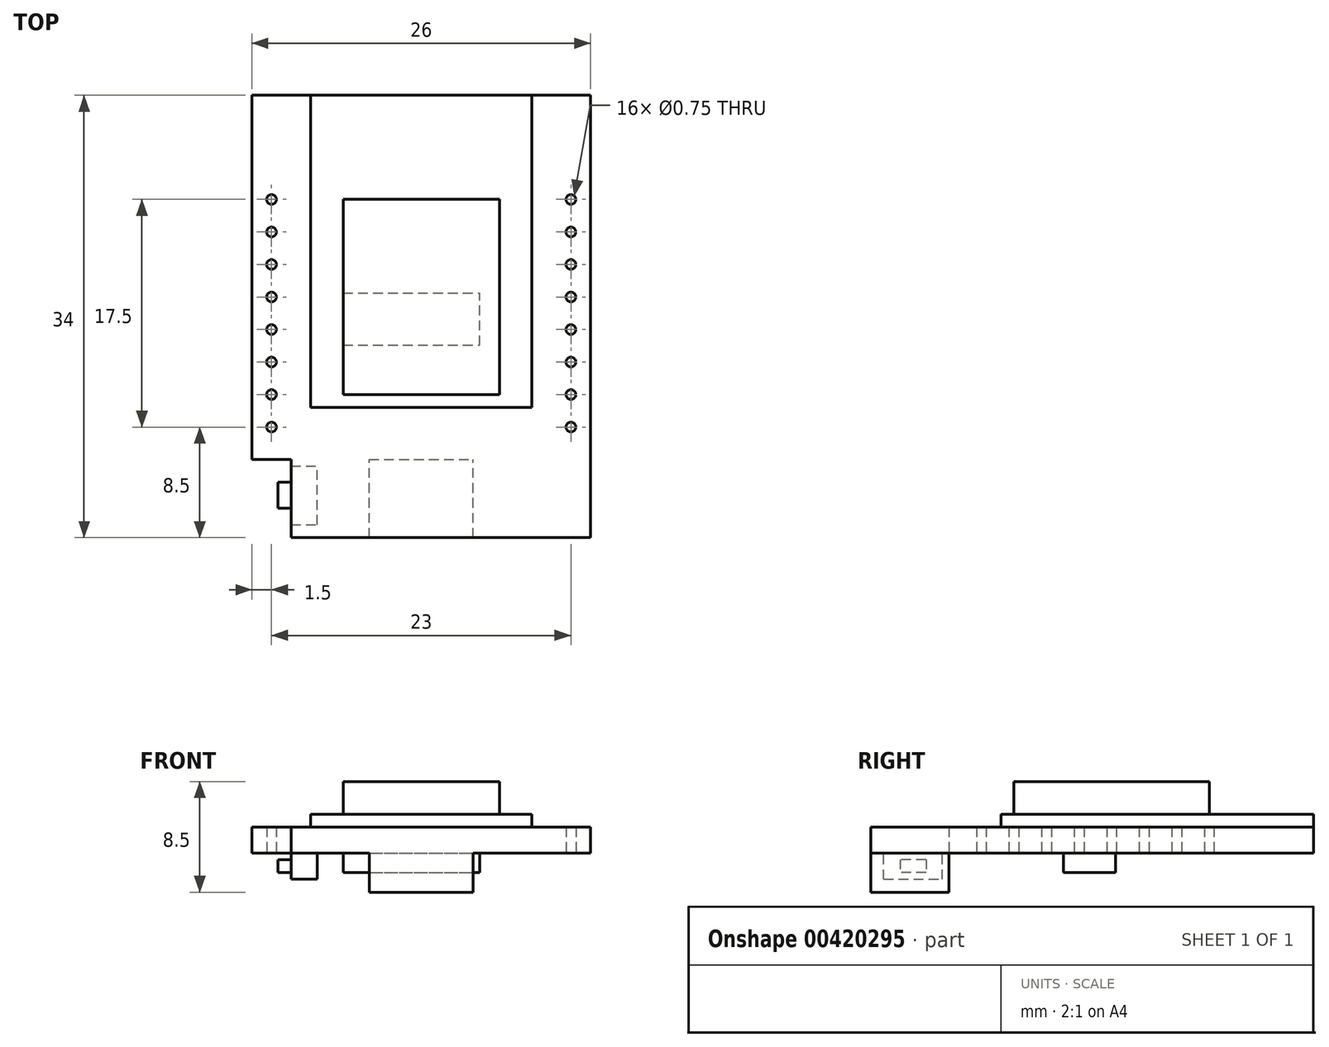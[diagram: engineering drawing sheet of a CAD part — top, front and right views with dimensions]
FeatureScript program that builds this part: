
annotation { "Feature Type Name" : "Feature", "Feature Type Description" : "" }
export const myFeature = defineFeature(function(context is Context, id is Id, definition is map)
    precondition{}
    {
        {
            var Q0;
            Q0=qCreatedBy(makeId("Top.planeOp"),FACE);
            var sketch = newSketch(context, id + "F0", { "sketchPlane" : qUnion([Q0])});
            skLineSegment(sketch, "E0.bottom", {"start": v(-13, 17) * mm, "end": v(13, 17) * mm});
            skLineSegment(sketch, "E0.top", {"start": v(-10, -17) * mm, "end": v(13, -17) * mm});
            skLineSegment(sketch, "E0.left", {"start": v(-13, 17) * mm, "end": v(-13, -11) * mm});
            skLineSegment(sketch, "E0.right", {"start": v(13, 17) * mm, "end": v(13, -17) * mm});
            skLineSegment(sketch, "E1.top", {"start": v(-13, -11) * mm, "end": v(-10, -11) * mm});
            skLineSegment(sketch, "E1.right", {"start": v(-10, -17) * mm, "end": v(-10, -11) * mm});
            skSolve(sketch);
        }
        {
            var Q0;
            Q0=qSketchRegion(id+"F0",true);
            extrude(context, id + "F1", {"entities" : qUnion([Q0]), "depth" : 2 * mm});
        }
        {
            var Q0;
            Q0=makeQuery(id+"F1.opExtrude","CAP_FACE",FACE,{"disambiguationData":[OSD([sQuery(id+"F0.wireOp",EDGE,"E0.bottom"),sQuery(id+"F0.wireOp",EDGE,"E0.top"),sQuery(id+"F0.wireOp",EDGE,"E0.left"),sQuery(id+"F0.wireOp",EDGE,"E0.right"),sQuery(id+"F0.wireOp",EDGE,"E1.bottom"),sQuery(id+"F0.wireOp",EDGE,"E1.left")])],"isStart":false});
            var sketch = newSketch(context, id + "F2", { "sketchPlane" : qUnion([Q0])});
            skLineSegment(sketch, "E2.bottom", {"start": v(-8.5, 17) * mm, "end": v(8.5, 17) * mm});
            skLineSegment(sketch, "E2.top", {"start": v(-8.5, -7) * mm, "end": v(8.5, -7) * mm});
            skLineSegment(sketch, "E2.left", {"start": v(-8.5, 17) * mm, "end": v(-8.5, -7) * mm});
            skLineSegment(sketch, "E2.right", {"start": v(8.5, 17) * mm, "end": v(8.5, -7) * mm});
            skSolve(sketch);
        }
        {
            var Q0;
            Q0=qSketchRegion(id+"F2",true);
            extrude(context, id + "F3", {"entities" : qUnion([Q0]), "operationType" : NewBodyOperationType.ADD, "depth" : 1 * mm});
        }
        {
            var Q0;
            Q0=makeQuery(id+"F3.opExtrude","CAP_FACE",FACE,{"disambiguationData":[OSD([sQuery(id+"F2.wireOp",EDGE,"E2.bottom"),sQuery(id+"F2.wireOp",EDGE,"E2.top"),sQuery(id+"F2.wireOp",EDGE,"E2.left"),sQuery(id+"F2.wireOp",EDGE,"E2.right")])],"isStart":false});
            var sketch = newSketch(context, id + "F4", { "sketchPlane" : qUnion([Q0])});
            skLineSegment(sketch, "E3.bottom", {"start": v(-6, 9) * mm, "end": v(6, 9) * mm});
            skLineSegment(sketch, "E3.top", {"start": v(-6, -6) * mm, "end": v(6, -6) * mm});
            skLineSegment(sketch, "E3.left", {"start": v(-6, 9) * mm, "end": v(-6, -6) * mm});
            skLineSegment(sketch, "E3.right", {"start": v(6, 9) * mm, "end": v(6, -6) * mm});
            skSolve(sketch);
        }
        {
            var Q0;
            Q0=qSketchRegion(id+"F4",true);
            extrude(context, id + "F5", {"entities" : qUnion([Q0]), "operationType" : NewBodyOperationType.ADD, "depth" : 2.5 * mm});
        }
        {
            var Q0;
            Q0=makeQuery(id+"F1.opExtrude","CAP_FACE",FACE,{"disambiguationData":[OSD([sQuery(id+"F0.wireOp",EDGE,"E0.bottom"),sQuery(id+"F0.wireOp",EDGE,"E0.top"),sQuery(id+"F0.wireOp",EDGE,"E0.left"),sQuery(id+"F0.wireOp",EDGE,"E0.right"),sQuery(id+"F0.wireOp",EDGE,"E1.top"),sQuery(id+"F0.wireOp",EDGE,"E1.right")])],"isStart":true});
            var sketch = newSketch(context, id + "F6", { "sketchPlane" : qUnion([Q0])});
            skLineSegment(sketch, "E4.bottom", {"start": v(-4, 17) * mm, "end": v(4, 17) * mm});
            skLineSegment(sketch, "E4.top", {"start": v(-4, 11) * mm, "end": v(4, 11) * mm});
            skLineSegment(sketch, "E4.left", {"start": v(-4, 17) * mm, "end": v(-4, 11) * mm});
            skLineSegment(sketch, "E4.right", {"start": v(4, 17) * mm, "end": v(4, 11) * mm});
            skSolve(sketch);
        }
        {
            var Q0;
            Q0=qSketchRegion(id+"F6",true);
            extrude(context, id + "F7", {"entities" : qUnion([Q0]), "operationType" : NewBodyOperationType.ADD, "depth" : 3 * mm});
        }
        {
            var Q0;
            Q0=makeQuery(id+"F1.opExtrude","CAP_FACE",FACE,{"disambiguationData":[OSD([sQuery(id+"F0.wireOp",EDGE,"E0.bottom"),sQuery(id+"F0.wireOp",EDGE,"E0.top"),sQuery(id+"F0.wireOp",EDGE,"E0.left"),sQuery(id+"F0.wireOp",EDGE,"E0.right"),sQuery(id+"F0.wireOp",EDGE,"E1.top"),sQuery(id+"F0.wireOp",EDGE,"E1.right")])],"isStart":true});
            var sketch = newSketch(context, id + "F8", { "sketchPlane" : qUnion([Q0])});
            skLineSegment(sketch, "E5.bottom", {"start": v(-10, 16) * mm, "end": v(-8, 16) * mm});
            skLineSegment(sketch, "E5.top", {"start": v(-10, 11.5) * mm, "end": v(-8, 11.5) * mm});
            skLineSegment(sketch, "E5.left", {"start": v(-10, 16) * mm, "end": v(-10, 11.5) * mm});
            skLineSegment(sketch, "E5.right", {"start": v(-8, 16) * mm, "end": v(-8, 11.5) * mm});
            skSolve(sketch);
        }
        {
            var Q0;
            Q0=qSketchRegion(id+"F8",true);
            extrude(context, id + "F9", {"entities" : qUnion([Q0]), "operationType" : NewBodyOperationType.ADD, "depth" : 2 * mm});
        }
        {
            var Q0;
            Q0=makeQuery(id+"F9.boolean.opBoolean","MERGE",FACE,{"derivedFrom":[makeQuery(id+"F1.opExtrude","SWEPT_FACE",FACE,{"disambiguationData":[OSD([sQuery(id+"F0.wireOp",EDGE,"E1.right")])]}),makeQuery(id+"F9.opExtrude","SWEPT_FACE",FACE,{"disambiguationData":[OSD([sQuery(id+"F8.wireOp",EDGE,"E5.left")])]})]});
            var sketch = newSketch(context, id + "F10", { "sketchPlane" : qUnion([Q0])});
            skLineSegment(sketch, "E6.bottom", {"start": v(12.75, -0.5) * mm, "end": v(14.75, -0.5) * mm});
            skLineSegment(sketch, "E6.top", {"start": v(12.75, -1.5) * mm, "end": v(14.75, -1.5) * mm});
            skLineSegment(sketch, "E6.left", {"start": v(12.75, -0.5) * mm, "end": v(12.75, -1.5) * mm});
            skLineSegment(sketch, "E6.right", {"start": v(14.75, -0.5) * mm, "end": v(14.75, -1.5) * mm});
            skSolve(sketch);
        }
        {
            var Q0;
            Q0=qSketchRegion(id+"F10",true);
            extrude(context, id + "F11", {"entities" : qUnion([Q0]), "operationType" : NewBodyOperationType.ADD, "depth" : 1 * mm});
        }
        {
            var Q0;
            Q0=makeQuery(id+"F1.opExtrude","CAP_FACE",FACE,{"disambiguationData":[OSD([sQuery(id+"F0.wireOp",EDGE,"E0.bottom"),sQuery(id+"F0.wireOp",EDGE,"E0.top"),sQuery(id+"F0.wireOp",EDGE,"E0.left"),sQuery(id+"F0.wireOp",EDGE,"E0.right"),sQuery(id+"F0.wireOp",EDGE,"E1.top"),sQuery(id+"F0.wireOp",EDGE,"E1.right")])],"isStart":true});
            var sketch = newSketch(context, id + "F12", { "sketchPlane" : qUnion([Q0])});
            skLineSegment(sketch, "E7.bottom", {"start": v(-6, 2.2) * mm, "end": v(4.5, 2.2) * mm});
            skLineSegment(sketch, "E7.top", {"start": v(-6, -1.8) * mm, "end": v(4.5, -1.8) * mm});
            skLineSegment(sketch, "E7.left", {"start": v(-6, 2.2) * mm, "end": v(-6, -1.8) * mm});
            skLineSegment(sketch, "E7.right", {"start": v(4.5, 2.2) * mm, "end": v(4.5, -1.8) * mm});
            skSolve(sketch);
        }
        {
            var Q0;
            Q0=qSketchRegion(id+"F12",true);
            extrude(context, id + "F13", {"entities" : qUnion([Q0]), "operationType" : NewBodyOperationType.ADD, "depth" : 1.5 * mm});
        }
        {
            var Q0;
            Q0=makeQuery(id+"F1.opExtrude","CAP_FACE",FACE,{"disambiguationData":[OSD([sQuery(id+"F0.wireOp",EDGE,"E0.bottom"),sQuery(id+"F0.wireOp",EDGE,"E0.top"),sQuery(id+"F0.wireOp",EDGE,"E0.left"),sQuery(id+"F0.wireOp",EDGE,"E0.right"),sQuery(id+"F0.wireOp",EDGE,"E1.top"),sQuery(id+"F0.wireOp",EDGE,"E1.right")])],"isStart":true});
            var sketch = newSketch(context, id + "F14", { "sketchPlane" : qUnion([Q0])});
            skCircle(sketch, "E8", {"center": v(-11.5, -9) * mm, "radius": 0.38 * mm});
            skCircle(sketch, "E9.0.1.0", {"center": v(-11.5, -6.5) * mm, "radius": 0.38 * mm});
            skCircle(sketch, "E9.0.2.0", {"center": v(-11.5, -4) * mm, "radius": 0.38 * mm});
            skCircle(sketch, "E9.0.3.0", {"center": v(-11.5, -1.5) * mm, "radius": 0.38 * mm});
            skCircle(sketch, "E9.0.4.0", {"center": v(-11.5, 1) * mm, "radius": 0.38 * mm});
            skCircle(sketch, "E9.0.5.0", {"center": v(-11.5, 3.5) * mm, "radius": 0.38 * mm});
            skCircle(sketch, "E9.0.6.0", {"center": v(-11.5, 6) * mm, "radius": 0.38 * mm});
            skCircle(sketch, "E9.0.7.0", {"center": v(-11.5, 8.5) * mm, "radius": 0.38 * mm});
            skLineSegment(sketch, "E9.direction1", {"start": v(-11.5, -9) * mm, "end": v(11.5, -9) * mm, "construction": true});
            skLineSegment(sketch, "E9.direction2", {"start": v(-11.5, -9) * mm, "end": v(-11.5, -6.5) * mm, "construction": true});
            skCircle(sketch, "E10.0.1.0", {"center": v(11.5, -9) * mm, "radius": 0.38 * mm});
            skCircle(sketch, "E10.0.1.1", {"center": v(11.5, -6.5) * mm, "radius": 0.38 * mm});
            skCircle(sketch, "E10.0.1.2", {"center": v(11.5, -4) * mm, "radius": 0.38 * mm});
            skCircle(sketch, "E10.0.1.3", {"center": v(11.5, -1.5) * mm, "radius": 0.38 * mm});
            skCircle(sketch, "E10.0.1.4", {"center": v(11.5, 1) * mm, "radius": 0.38 * mm});
            skCircle(sketch, "E10.0.1.5", {"center": v(11.5, 3.5) * mm, "radius": 0.38 * mm});
            skCircle(sketch, "E10.0.1.6", {"center": v(11.5, 6) * mm, "radius": 0.38 * mm});
            skCircle(sketch, "E10.0.1.7", {"center": v(11.5, 8.5) * mm, "radius": 0.38 * mm});
            skSolve(sketch);
        }
        {
            var Q0;
            Q0=qSketchRegion(id+"F14",true);
            extrude(context, id + "F15", {"entities" : qUnion([Q0]), "operationType" : NewBodyOperationType.REMOVE, "oppositeDirection" : true, "depth" : 25 * mm});
        }
    });
